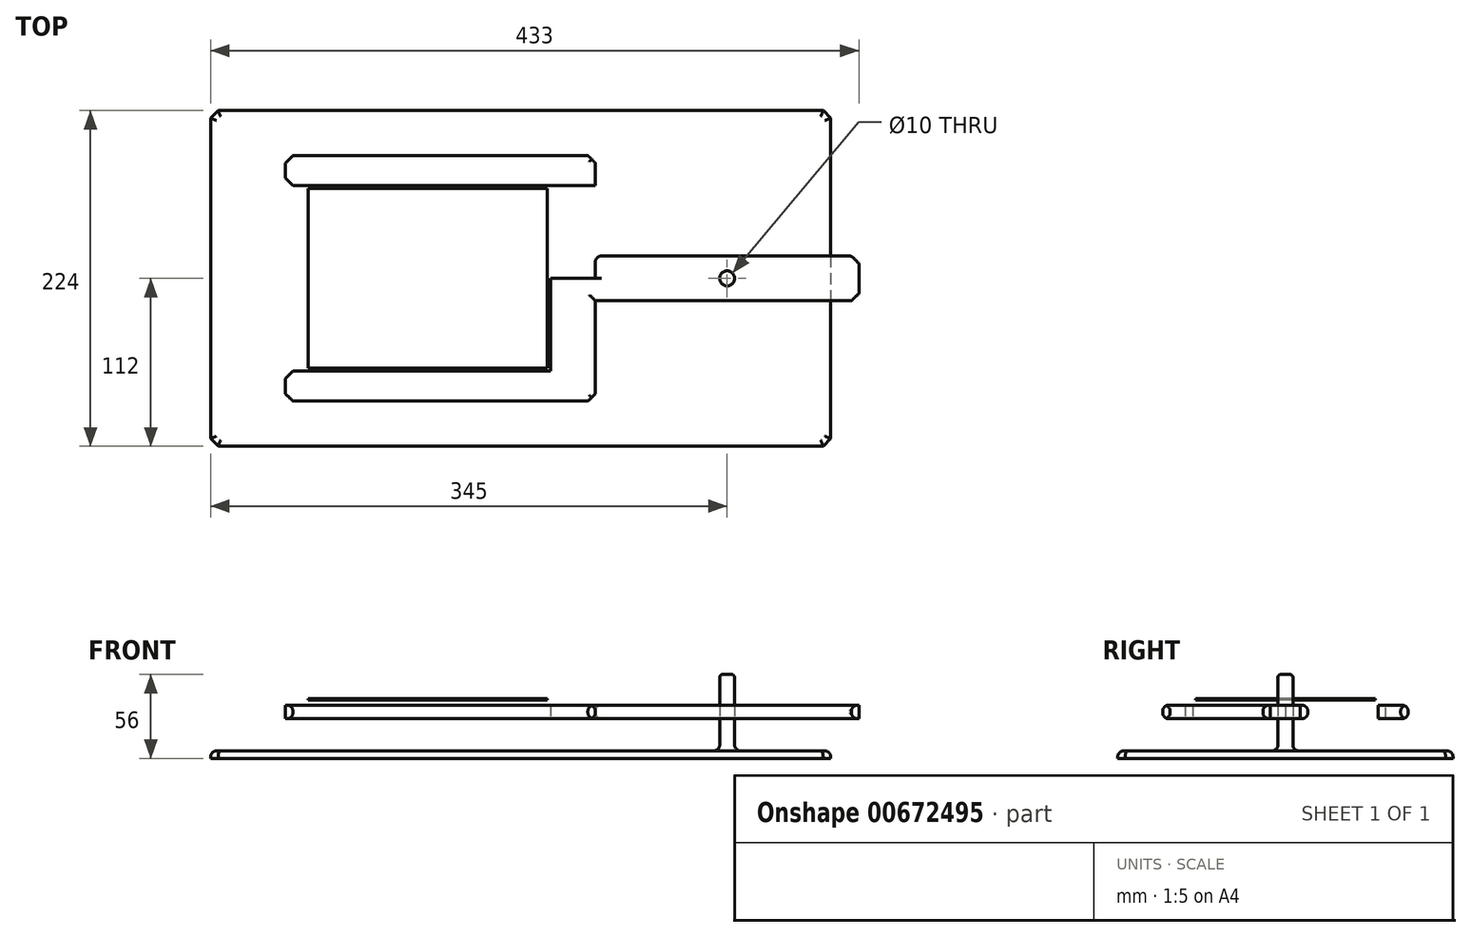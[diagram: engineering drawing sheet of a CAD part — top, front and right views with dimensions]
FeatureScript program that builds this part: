
annotation { "Feature Type Name" : "Feature", "Feature Type Description" : "" }
export const myFeature = defineFeature(function(context is Context, id is Id, definition is map)
    precondition{}
    {
        {
            var Q0;
            Q0=qCreatedBy(makeId("Top.planeOp"),FACE);
            var sketch = newSketch(context, id + "F0", { "sketchPlane" : qUnion([Q0])});
            skLineSegment(sketch, "E0", {"start": v(-90, 0) * mm, "end": v(0, 0) * mm});
            skLineSegment(sketch, "E1.bottom", {"start": v(-90, 60) * mm, "end": v(70, 60) * mm});
            skLineSegment(sketch, "E1.top", {"start": v(-90, -60) * mm, "end": v(70, -60) * mm});
            skLineSegment(sketch, "E1.left", {"start": v(-90, 60) * mm, "end": v(-90, -60) * mm});
            skLineSegment(sketch, "E1.right", {"start": v(70, 60) * mm, "end": v(70, -60) * mm});
            skPoint(sketch, "E1.middle", {"position": v(-10, 0) * mm});
            skLineSegment(sketch, "E2.bottom", {"start": v(-105, 62) * mm, "end": v(102, 62) * mm});
            skLineSegment(sketch, "E2.top", {"start": v(-105, 82) * mm, "end": v(102, 82) * mm});
            skLineSegment(sketch, "E2.left", {"start": v(-105, 62) * mm, "end": v(-105, 82) * mm});
            skLineSegment(sketch, "E2.right", {"start": v(102, 62) * mm, "end": v(102, 82) * mm});
            skLineSegment(sketch, "E3.bottom", {"start": v(102, 62) * mm, "end": v(72, 62) * mm});
            skLineSegment(sketch, "E3.top", {"start": v(102, 0) * mm, "end": v(72, 0) * mm});
            skLineSegment(sketch, "E3.left", {"start": v(102, 62) * mm, "end": v(102, 0) * mm});
            skLineSegment(sketch, "E3.right", {"start": v(72, 62) * mm, "end": v(72, 0) * mm});
            skLineSegment(sketch, "E4.MirrorCS", {"start": v(102, -62) * mm, "end": v(72, -62) * mm});
            skLineSegment(sketch, "E5.MirrorCS", {"start": v(102, -62) * mm, "end": v(102, 0) * mm});
            skLineSegment(sketch, "E6.MirrorCS", {"start": v(72, -62) * mm, "end": v(72, 0) * mm});
            skLineSegment(sketch, "E7.MirrorCS", {"start": v(-105, -62) * mm, "end": v(102, -62) * mm});
            skLineSegment(sketch, "E8.MirrorCS", {"start": v(102, -62) * mm, "end": v(102, -82) * mm});
            skLineSegment(sketch, "E9.MirrorCS", {"start": v(-105, -82) * mm, "end": v(102, -82) * mm});
            skLineSegment(sketch, "E10.MirrorCS", {"start": v(-105, -62) * mm, "end": v(-105, -82) * mm});
            skLineSegment(sketch, "E11.bottom", {"start": v(102, 15) * mm, "end": v(278, 15) * mm});
            skLineSegment(sketch, "E11.top", {"start": v(102, -15) * mm, "end": v(278, -15) * mm});
            skLineSegment(sketch, "E11.left", {"start": v(102, 15) * mm, "end": v(102, -15) * mm});
            skLineSegment(sketch, "E11.right", {"start": v(278, 15) * mm, "end": v(278, -15) * mm});
            skPoint(sketch, "E11.middle", {"position": v(190, 0) * mm});
            skLineSegment(sketch, "E12", {"start": v(190, 37.07) * mm, "end": v(190, 158.55) * mm});
            skPoint(sketch, "E12.startSnap0", {"position": v(190, 15) * mm});
            skLineSegment(sketch, "E13.MirrorCS", {"start": v(308, -62) * mm, "end": v(308, 0) * mm});
            skLineSegment(sketch, "E14.MirrorCS", {"start": v(308, 62) * mm, "end": v(308, 0) * mm});
            skLineSegment(sketch, "E15.MirrorCS", {"start": v(485, -62) * mm, "end": v(485, -82) * mm});
            skPoint(sketch, "E16.MirrorP", {"position": v(390, 0) * mm});
            skLineSegment(sketch, "E17.MirrorCS", {"start": v(310, 60) * mm, "end": v(310, -60) * mm});
            skLineSegment(sketch, "E18.MirrorCS", {"start": v(485, 62) * mm, "end": v(485, 82) * mm});
            skLineSegment(sketch, "E19.MirrorCS", {"start": v(470, 60) * mm, "end": v(310, 60) * mm});
            skLineSegment(sketch, "E20.MirrorCS", {"start": v(470, -60) * mm, "end": v(310, -60) * mm});
            skLineSegment(sketch, "E21.MirrorCS", {"start": v(470, 60) * mm, "end": v(470, -60) * mm});
            skLineSegment(sketch, "E22.MirrorCS", {"start": v(485, -82) * mm, "end": v(278, -82) * mm});
            skLineSegment(sketch, "E23.MirrorCS", {"start": v(485, -62) * mm, "end": v(278, -62) * mm});
            skLineSegment(sketch, "E24.MirrorCS", {"start": v(278, 0) * mm, "end": v(308, 0) * mm});
            skLineSegment(sketch, "E25.MirrorCS", {"start": v(278, 62) * mm, "end": v(308, 62) * mm});
            skLineSegment(sketch, "E26.MirrorCS", {"start": v(485, 82) * mm, "end": v(278, 82) * mm});
            skLineSegment(sketch, "E27.MirrorCS", {"start": v(278, 62) * mm, "end": v(278, 82) * mm});
            skLineSegment(sketch, "E28.MirrorCS", {"start": v(278, -62) * mm, "end": v(278, -82) * mm});
            skLineSegment(sketch, "E29.MirrorCS", {"start": v(485, 62) * mm, "end": v(278, 62) * mm});
            skLineSegment(sketch, "E30.MirrorCS", {"start": v(278, 62) * mm, "end": v(278, 0) * mm});
            skLineSegment(sketch, "E31.MirrorCS", {"start": v(278, -62) * mm, "end": v(278, 0) * mm});
            skCircle(sketch, "E32", {"center": v(190, 0) * mm, "radius": 5 * mm});
            skSolve(sketch);
        }
        {
            var Q0;
            Q0=makeQuery(id+"F0.imprint","IMPRINT",FACE,{"disambiguationData":[TD([[makeQuery(id+"F0.imprint","IMPRINT",EDGE,{"derivedFrom":sQuery(id+"F0.wireOp",EDGE,"E2.bottom")}),1.0]])]});
            var Q1;
            Q1=makeQuery(id+"F0.imprint","IMPRINT",FACE,{"disambiguationData":[TD([[makeQuery(id+"F0.imprint","IMPRINT",EDGE,{"derivedFrom":sQuery(id+"F0.wireOp",EDGE,"E3.bottom")}),1.0]])]});
            var Q2;
            {var subQ3=sQuery(id+"F0.wireOp",EDGE,"E3.top");Q2=makeQuery(id+"F0.imprint","IMPRINT",FACE,{"disambiguationData":[TD([[makeQuery(id+"F0.imprint","IMPRINT",EDGE,{"derivedFrom":subQ3}),1.0]])]});}
            var Q3;
            {var subQ0=sQuery(id+"F0.wireOp",EDGE,"E8.MirrorCS");Q3=makeQuery(id+"F0.imprint","IMPRINT",FACE,{"disambiguationData":[TD([[makeQuery(id+"F0.imprint","IMPRINT",EDGE,{"derivedFrom":subQ0}),-1.0]])]});}
            var Q4;
            {var subQ3=sQuery(id+"F0.wireOp",EDGE,"E11.bottom");Q4=makeQuery(id+"F0.imprint","IMPRINT",FACE,{"disambiguationData":[TD([[makeQuery(id+"F0.imprint","IMPRINT",EDGE,{"derivedFrom":subQ3}),-1.0]])]});}
            extrude(context, id + "F1", {"entities" : qUnion([Q0, Q1, Q2, Q3, Q4]), "endBound" : BoundingType.SYMMETRIC, "depth" : 9 * mm, "offsetDistance" : 25 * mm});
        }
        {
            var Q0;
            Q0=makeQuery(id+"F0.imprint","IMPRINT",FACE,{"disambiguationData":[TD([[makeQuery(id+"F0.imprint","IMPRINT",EDGE,{"derivedFrom":sQuery(id+"F0.wireOp",EDGE,"E32")}),1.0]])]});
            extrude(context, id + "F2", {"entities" : qUnion([Q0]), "depth" : 25 * mm, "offsetDistance" : 25 * mm, "hasSecondDirection" : true, "secondDirectionOppositeDirection" : true, "secondDirectionDepth" : 26 * mm});
        }
        {
            var Q0;
            Q0=makeQuery(id+"F2.opExtrude","CAP_FACE",FACE,{"disambiguationData":[OSD([sQuery(id+"F0.wireOp",EDGE,"E32")])],"isStart":true});
            var sketch = newSketch(context, id + "F3", { "sketchPlane" : qUnion([Q0])});
            skLineSegment(sketch, "E33.bottom", {"start": v(535, 112) * mm, "end": v(-155, 112) * mm});
            skLineSegment(sketch, "E33.top", {"start": v(535, -112) * mm, "end": v(-155, -112) * mm});
            skLineSegment(sketch, "E33.left", {"start": v(535, 112) * mm, "end": v(535, -112) * mm});
            skLineSegment(sketch, "E33.right", {"start": v(-155, 112) * mm, "end": v(-155, -112) * mm});
            skPoint(sketch, "E33.middle", {"position": v(190, 0) * mm});
            skLineSegment(sketch, "E34", {"start": v(259.17, -112) * mm, "end": v(259.17, 112) * mm});
            skSolve(sketch);
        }
        {
            var Q0;
            Q0=makeQuery(id+"F3.imprint","IMPRINT",FACE,{"disambiguationData":[TD([[makeQuery(id+"F3.imprint","IMPRINT",EDGE,{"derivedFrom":makeQuery(id+"F2.opExtrude","CAP_EDGE",EDGE,{"disambiguationData":[OSD([sQuery(id+"F0.wireOp",EDGE,"E32")])],"isStart":true})}),-1.0]])]});
            var Q1;
            {var subQ0=sQuery(id+"F3.wireOp",EDGE,"E33.right");Q1=makeQuery(id+"F3.imprint","IMPRINT",FACE,{"disambiguationData":[TD([[makeQuery(id+"F3.imprint","IMPRINT",EDGE,{"derivedFrom":subQ0}),1.0]])]});}
            extrude(context, id + "F4", {"entities" : qUnion([Q0, Q1]), "operationType" : NewBodyOperationType.ADD, "depth" : 5 * mm, "offsetDistance" : 25 * mm});
        }
        {
            var Q0;
            {var subQ3=sQuery(id+"F0.wireOp",EDGE,"E1.bottom");Q0=makeQuery(id+"F0.imprint","IMPRINT",FACE,{"disambiguationData":[TD([[makeQuery(id+"F0.imprint","IMPRINT",EDGE,{"derivedFrom":subQ3}),-1.0]])]});}
            extrude(context, id + "F5", {"entities" : qUnion([Q0]), "depth" : 9 * mm, "offsetDistance" : 25 * mm, "hasSecondDirection" : true, "secondDirectionOppositeDirection" : false, "secondDirectionDepth" : 8 * mm});
        }
        {
            var Q0;
            Q0=makeQuery(id+"F1.opExtrude","SWEPT_EDGE",EDGE,{"disambiguationData":[OSD([sQuery(id+"F0.wireOp",EDGE,"E2.bottom"),sQuery(id+"F0.wireOp",EDGE,"E2.left")])]});
            var Q1;
            Q1=makeQuery(id+"F1.opExtrude","SWEPT_EDGE",EDGE,{"disambiguationData":[OSD([sQuery(id+"F0.wireOp",EDGE,"E2.top"),sQuery(id+"F0.wireOp",EDGE,"E2.left")])]});
            var Q2;
            Q2=makeQuery(id+"F1.opExtrude","SWEPT_EDGE",EDGE,{"disambiguationData":[OSD([sQuery(id+"F0.wireOp",EDGE,"E9.MirrorCS"),sQuery(id+"F0.wireOp",EDGE,"E10.MirrorCS")])]});
            var Q3;
            Q3=makeQuery(id+"F1.opExtrude","SWEPT_EDGE",EDGE,{"disambiguationData":[OSD([sQuery(id+"F0.wireOp",EDGE,"E7.MirrorCS"),sQuery(id+"F0.wireOp",EDGE,"E10.MirrorCS")])]});
            var Q4;
            Q4=makeQuery(id+"F1.opExtrude","SWEPT_EDGE",EDGE,{"disambiguationData":[OSD([sQuery(id+"F0.wireOp",EDGE,"E11.top"),sQuery(id+"F0.wireOp",EDGE,"E31.MirrorCS")])]});
            var Q5;
            Q5=makeQuery(id+"F1.opExtrude","SWEPT_EDGE",EDGE,{"disambiguationData":[OSD([sQuery(id+"F0.wireOp",EDGE,"E11.bottom"),sQuery(id+"F0.wireOp",EDGE,"E30.MirrorCS")])]});
            var Q6;
            Q6=makeQuery(id+"F1.opExtrude","SWEPT_EDGE",EDGE,{"disambiguationData":[OSD([sQuery(id+"F0.wireOp",EDGE,"E8.MirrorCS"),sQuery(id+"F0.wireOp",EDGE,"E9.MirrorCS")])]});
            var Q7;
            Q7=makeQuery(id+"F1.opExtrude","SWEPT_EDGE",EDGE,{"disambiguationData":[OSD([sQuery(id+"F0.wireOp",EDGE,"E2.top"),sQuery(id+"F0.wireOp",EDGE,"E2.right")])]});
            var Q8;
            Q8=makeQuery(id+"F4.opExtrude","SWEPT_EDGE",EDGE,{"disambiguationData":[OSD([sQuery(id+"F3.wireOp",EDGE,"E33.top"),sQuery(id+"F3.wireOp",EDGE,"E33.right")])]});
            var Q9;
            Q9=makeQuery(id+"F4.opExtrude","SWEPT_EDGE",EDGE,{"disambiguationData":[OSD([sQuery(id+"F3.wireOp",EDGE,"E33.bottom"),sQuery(id+"F3.wireOp",EDGE,"E33.right")])]});
            var Q10;
            Q10=makeQuery(id+"F4.opExtrude","SWEPT_EDGE",EDGE,{"disambiguationData":[OSD([sQuery(id+"F3.wireOp",EDGE,"E33.top"),sQuery(id+"F3.wireOp",EDGE,"E34")])]});
            var Q11;
            Q11=makeQuery(id+"F4.opExtrude","SWEPT_EDGE",EDGE,{"disambiguationData":[OSD([sQuery(id+"F3.wireOp",EDGE,"E33.bottom"),sQuery(id+"F3.wireOp",EDGE,"E34")])]});
            chamfer(context, id + "F6", {"entities" : qUnion([Q0, Q1, Q2, Q3, Q4, Q5, Q6, Q7, Q8, Q9, Q10, Q11]), "width" : 5 * mm, "tangentPropagation" : true});
        }
        {
            var Q0;
            Q0=makeQuery(id+"F1.opExtrude","CAP_EDGE",EDGE,{"disambiguationData":[OSD([sQuery(id+"F0.wireOp",EDGE,"E11.bottom")])],"isStart":false});
            var Q1;
            Q1=makeQuery(id+"F1.opExtrude","CAP_EDGE",EDGE,{"disambiguationData":[OSD([sQuery(id+"F0.wireOp",EDGE,"E30.MirrorCS"),sQuery(id+"F0.wireOp",EDGE,"E31.MirrorCS")])],"isStart":false});
            var Q2;
            Q2=makeQuery(id+"F1.opExtrude","CAP_EDGE",EDGE,{"disambiguationData":[OSD([sQuery(id+"F0.wireOp",EDGE,"E11.top")])],"isStart":false});
            var Q3;
            Q3=makeQuery(id+"F1.opExtrude","CAP_EDGE",EDGE,{"disambiguationData":[OSD([sQuery(id+"F0.wireOp",EDGE,"E5.MirrorCS"),sQuery(id+"F0.wireOp",EDGE,"E8.MirrorCS")])],"isStart":false});
            var Q4;
            Q4=makeQuery(id+"F1.opExtrude","CAP_EDGE",EDGE,{"disambiguationData":[OSD([sQuery(id+"F0.wireOp",EDGE,"E2.right"),sQuery(id+"F0.wireOp",EDGE,"E3.left")])],"isStart":false});
            var Q5;
            Q5=makeQuery(id+"F1.opExtrude","CAP_EDGE",EDGE,{"disambiguationData":[OSD([sQuery(id+"F0.wireOp",EDGE,"E2.right"),sQuery(id+"F0.wireOp",EDGE,"E3.left")])],"isStart":true});
            var Q6;
            Q6=makeQuery(id+"F1.opExtrude","SWEPT_FACE",FACE,{"disambiguationData":[OSD([sQuery(id+"F0.wireOp",EDGE,"E11.bottom")])]});
            var Q7;
            Q7=makeQuery(id+"F1.opExtrude","CAP_EDGE",EDGE,{"disambiguationData":[OSD([sQuery(id+"F0.wireOp",EDGE,"E11.top")])],"isStart":true});
            var Q8;
            Q8=makeQuery(id+"F1.opExtrude","CAP_EDGE",EDGE,{"disambiguationData":[OSD([sQuery(id+"F0.wireOp",EDGE,"E30.MirrorCS"),sQuery(id+"F0.wireOp",EDGE,"E31.MirrorCS")])],"isStart":true});
            var Q9;
            Q9=makeQuery(id+"F1.opExtrude","CAP_EDGE",EDGE,{"disambiguationData":[OSD([sQuery(id+"F0.wireOp",EDGE,"E5.MirrorCS"),sQuery(id+"F0.wireOp",EDGE,"E8.MirrorCS")])],"isStart":true});
            var Q10;
            Q10=makeQuery(id+"F1.opExtrude","CAP_EDGE",EDGE,{"disambiguationData":[OSD([sQuery(id+"F0.wireOp",EDGE,"E9.MirrorCS")])],"isStart":false});
            var Q11;
            Q11=makeQuery(id+"F1.opExtrude","CAP_EDGE",EDGE,{"disambiguationData":[OSD([sQuery(id+"F0.wireOp",EDGE,"E9.MirrorCS")])],"isStart":true});
            var Q12;
            Q12=makeQuery(id+"F1.opExtrude","CAP_EDGE",EDGE,{"disambiguationData":[OSD([sQuery(id+"F0.wireOp",EDGE,"E2.top")])],"isStart":false});
            var Q13;
            Q13=makeQuery(id+"F1.opExtrude","CAP_EDGE",EDGE,{"disambiguationData":[OSD([sQuery(id+"F0.wireOp",EDGE,"E2.top")])],"isStart":true});
            var Q14;
            Q14=makeQuery(id+"F4.opExtrude","CAP_FACE",FACE,{"disambiguationData":[OSD([sQuery(id+"F3.wireOp",EDGE,"E33.bottom"),sQuery(id+"F3.wireOp",EDGE,"E33.top"),sQuery(id+"F3.wireOp",EDGE,"E33.right"),sQuery(id+"F3.wireOp",EDGE,"E34")])],"isStart":true});
            fillet(context, id + "F7", {"entities" : qUnion([Q0, Q1, Q2, Q3, Q4, Q5, Q6, Q7, Q8, Q9, Q10, Q11, Q12, Q13, Q14]), "radius" : 4 * mm, "tangentPropagation" : true, "allowEdgeOverflow" : false});
        }
        {
            var Q0;
            Q0=makeQuery(id+"F2.opExtrude","CAP_EDGE",EDGE,{"disambiguationData":[OSD([sQuery(id+"F0.wireOp",EDGE,"E32")])],"isStart":false});
            fillet(context, id + "F8", {"entities" : qUnion([Q0]), "radius" : 2 * mm, "tangentPropagation" : true, "allowEdgeOverflow" : false});
        }
    });
